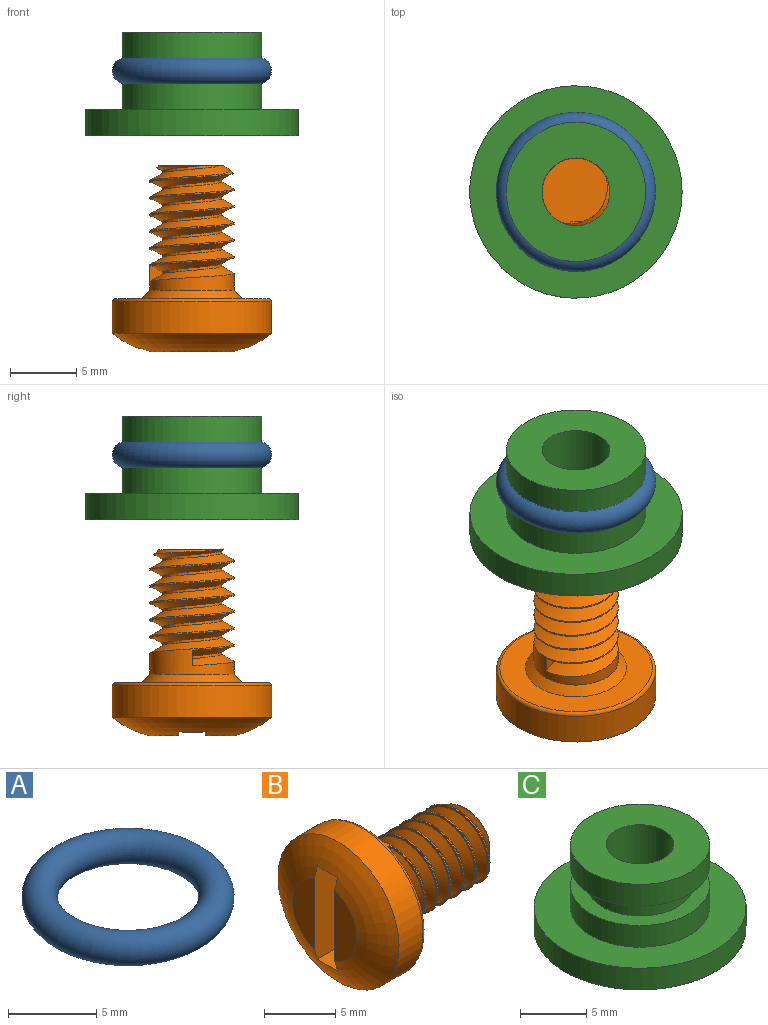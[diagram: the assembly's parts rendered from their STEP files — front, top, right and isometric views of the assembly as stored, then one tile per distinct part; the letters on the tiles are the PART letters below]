
ASSEMBLY  parts=3 mates=2
PART A: 1 faces, bbox 13x13x2 mm
  f0: torus R=5mm, axis (0,0,1), area 197.4mm2
PART B: 25 faces, bbox 14.6x13.1x13.1 mm
  f0: torus R=1.59mm, axis (1,0,0), area 88.6mm2, adj f1,f11,f12,f20,f21,f22,f23
  f1: plane 6.03x2.18mm, normal (-1,0,0), area 9.6mm2, adj f0,f22
  f2: plane 5.01x5.01mm, normal (1,0,0), area 19mm2, adj f9,f15,f17,f18
  f3: cylinder r=3.17mm len=6.35mm, axis (1,0,0), area 26.3mm2, adj f4,f13,f14,f15,f16
  f4: cylinder r=3.17mm len=6.35mm, axis (1,0,0), area 2mm2, adj f3,f5,f15,f16
  f5: cylinder r=3.17mm len=6.35mm, axis (1,0,0), area 2mm2, adj f4,f6,f15,f16
  f6: cylinder r=3.17mm len=6.35mm, axis (1,0,0), area 2mm2, adj f5,f7,f15,f16
  f7: cylinder r=3.17mm len=6.35mm, axis (1,0,0), area 2mm2, adj f6,f8,f15,f16
  f8: cylinder r=3.17mm len=6.35mm, axis (1,0,0), area 1.8mm2, adj f7,f9,f15,f16
  f9: cone r=2.54mm half-angle=45deg, axis (-1,0,0), area 4.7mm2, adj f2,f8,f15,f16,f17
  f10: plane 11.49x11.49mm, normal (1,0,0), area 58.1mm2, adj f13,f19
  f11: cylinder r=6mm len=12mm, axis (1,0,0), area 89.3mm2, adj f0,f19
  f12: plane 6.03x2.18mm, normal (-1,0,0), area 9.6mm2, adj f0,f20
  f13: cone r=3.17mm half-angle=45deg, axis (-1,0,0), area 19.7mm2, adj f3,f10
  f14: plane 1.17x0.93mm, normal (0,-1,0), area 0.7mm2, adj f3,f15,f16,f17,f18
  f15: bspline ~9x7.33mm, area 118.5mm2, adj f2,f3,f4,f5,f6,f7,f8,f9
  f16: bspline ~7.33x7.2mm, area 18.6mm2, adj f3,f4,f5,f6,f7,f8,f9,f14
  f17: bspline ~8.48x6.93mm, area 86mm2, adj f2,f9,f14,f16,f18
  f18: cylinder r=2.25mm len=8.2mm, axis (1,0,0), area 22.6mm2, adj f2,f14,f15,f17
  f19: torus R=5.75mm, axis (1,0,0), area 14.8mm2, adj f10,f11
  f20: plane 8.04x3.04mm, normal (0,1,0), area 23.7mm2, adj f0,f12,f21,f23,f24
  f21: plane 2.75x2mm, normal (0,0,-1), area 5.5mm2, adj f0,f20,f22,f24
  f22: plane 8.04x3.04mm, normal (0,-1,0), area 23.7mm2, adj f0,f1,f21,f23,f24
  f23: plane 2.82x2.07mm, normal (0,0,1), area 5.5mm2, adj f0,f20,f22,f24
  f24: plane 8x2mm, normal (-1,0,0), area 16mm2, adj f20,f21,f22,f23
PART C: 10 faces, bbox 16x16x7.8 mm
  f0: plane 10.5x10.5mm, normal (0,0,1), area 66.1mm2, adj f1,f9
  f1: cylinder r=5.25mm len=10.5mm, axis (0,0,1), area 66mm2, adj f0,f2
  f2: plane 10.5x10.5mm, normal (0,0,-1), area 36.3mm2, adj f1,f3
  f3: cylinder r=4mm len=8mm, axis (0,0,1), area 45.2mm2, adj f2,f4
  f4: plane 10.5x10.5mm, normal (0,0,1), area 36.3mm2, adj f3,f5
  f5: cylinder r=5.25mm len=10.5mm, axis (0,0,1), area 66mm2, adj f4,f6
  f6: plane 16x16mm, normal (0,0,1), area 114.5mm2, adj f5,f7
  f7: cylinder r=8mm len=16mm, axis (0,0,1), area 100.5mm2, adj f6,f8
  f8: plane 16x16mm, normal (0,0,-1), area 180.6mm2, adj f7,f9
  f9: cylinder r=2.55mm len=7.8mm, axis (0,0,-1), area 125.1mm2, adj f0,f8
PLACE A t=(-2.86,-1.51,7.33)mm
PLACE B rot(axis=(0,-1,0),90deg) t=(-2.86,-1.51,0.17)mm
PLACE C t=(-2.86,-1.51,2.43)mm
MATE cylindrical B.f0 <-> C.f1  axis (0,0,1) through (-2.86,-1.51,0.17)mm
MATE revolute A.f0 <-> C.f1  axis (0,0,1) through (-2.86,-1.51,7.33)mm
